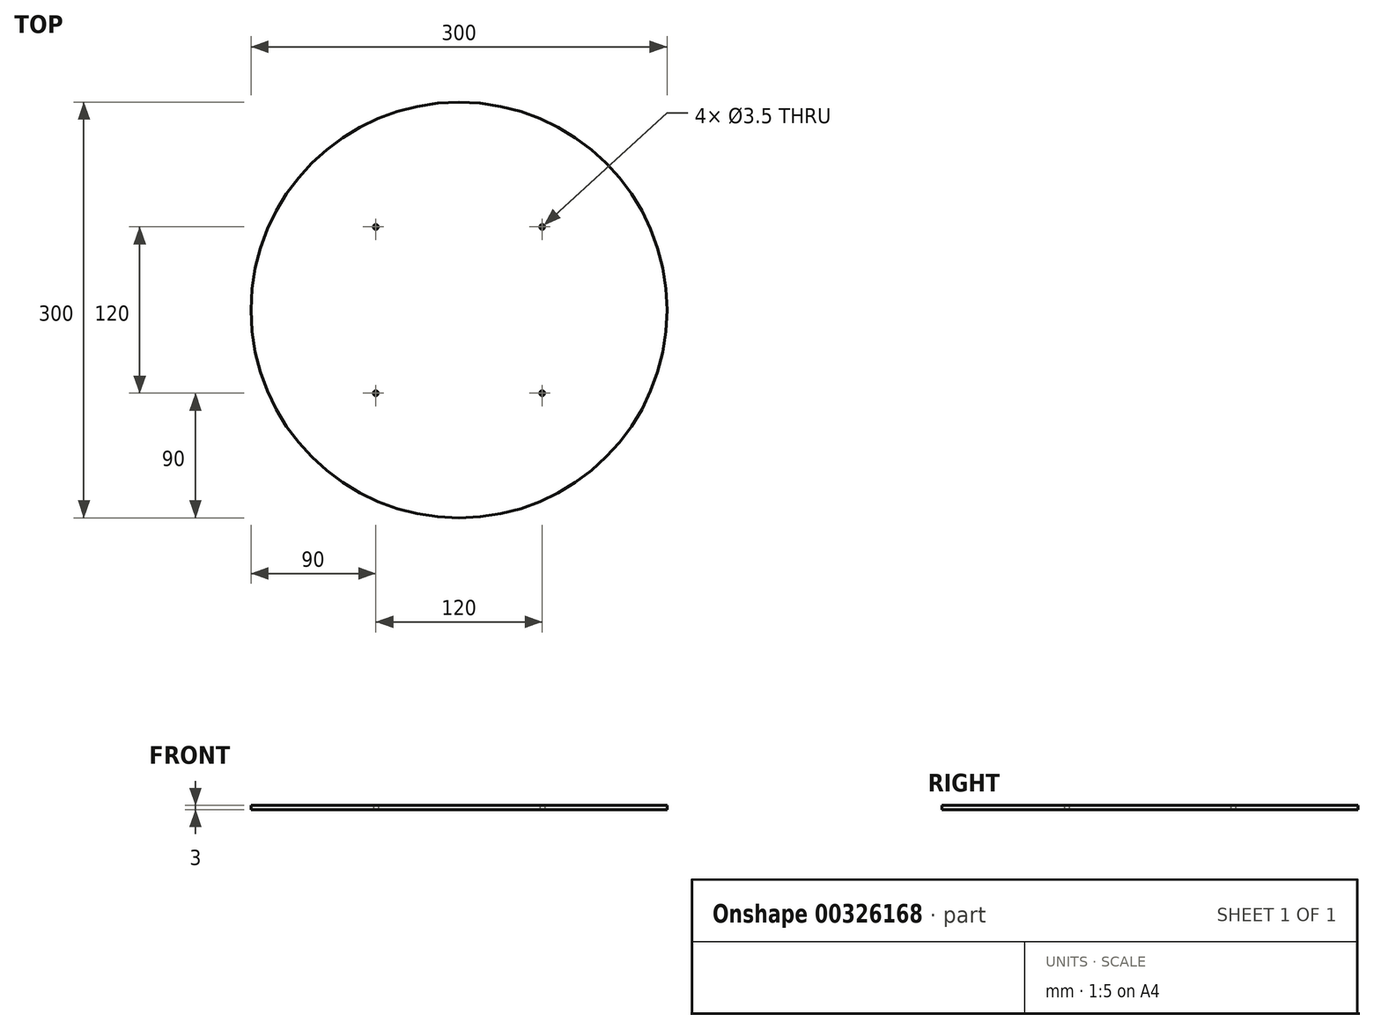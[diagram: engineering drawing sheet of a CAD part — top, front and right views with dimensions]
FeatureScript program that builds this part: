
annotation { "Feature Type Name" : "Feature", "Feature Type Description" : "" }
export const myFeature = defineFeature(function(context is Context, id is Id, definition is map)
    precondition{}
    {
        {
            var Q0;
            Q0=qCreatedBy(makeId("Top.planeOp"),FACE);
            var sketch = newSketch(context, id + "F0", { "sketchPlane" : qUnion([Q0])});
            skCircle(sketch, "E0", {"center": v(0, 0) * mm, "radius": 150 * mm});
            skLineSegment(sketch, "E1", {"start": v(106.07, 106.07) * mm, "end": v(-106.07, -106.07) * mm, "construction": true});
            skLineSegment(sketch, "E2", {"start": v(-106.07, 106.07) * mm, "end": v(106.07, -106.07) * mm, "construction": true});
            skLineSegment(sketch, "E3.bottom", {"start": v(-90, 90) * mm, "end": v(90, 90) * mm, "construction": true});
            skLineSegment(sketch, "E3.top", {"start": v(-90, -90) * mm, "end": v(90, -90) * mm, "construction": true});
            skLineSegment(sketch, "E3.left", {"start": v(-90, 90) * mm, "end": v(-90, -90) * mm, "construction": true});
            skLineSegment(sketch, "E3.right", {"start": v(90, 90) * mm, "end": v(90, -90) * mm, "construction": true});
            skLineSegment(sketch, "E4.bottom", {"start": v(-60, 60) * mm, "end": v(60, 60) * mm, "construction": true});
            skLineSegment(sketch, "E4.top", {"start": v(-60, -60) * mm, "end": v(60, -60) * mm, "construction": true});
            skLineSegment(sketch, "E4.left", {"start": v(-60, 60) * mm, "end": v(-60, -60) * mm, "construction": true});
            skLineSegment(sketch, "E4.right", {"start": v(60, 60) * mm, "end": v(60, -60) * mm, "construction": true});
            skCircle(sketch, "E5", {"center": v(60, 60) * mm, "radius": 1.75 * mm});
            skCircle(sketch, "E6.1.0", {"center": v(60, -60) * mm, "radius": 1.75 * mm});
            skCircle(sketch, "E6.2.0", {"center": v(-60, -60) * mm, "radius": 1.75 * mm});
            skCircle(sketch, "E6.3.0", {"center": v(-60, 60) * mm, "radius": 1.75 * mm});
            skLineSegment(sketch, "E6.anchor1", {"start": v(0, 0) * mm, "end": v(60, 60) * mm, "construction": true});
            skLineSegment(sketch, "E6.anchor2", {"start": v(0, 0) * mm, "end": v(-60, 60) * mm, "construction": true});
            skSolve(sketch);
        }
        {
            var Q0;
            Q0=makeQuery(id+"F0.imprint","IMPRINT",FACE,{"disambiguationData":[TD([[makeQuery(id+"F0.imprint","IMPRINT",EDGE,{"derivedFrom":sQuery(id+"F0.wireOp",EDGE,"E0")}),1.0]])]});
            extrude(context, id + "F1", {"entities" : qUnion([Q0]), "depth" : 3 * mm});
        }
    });
